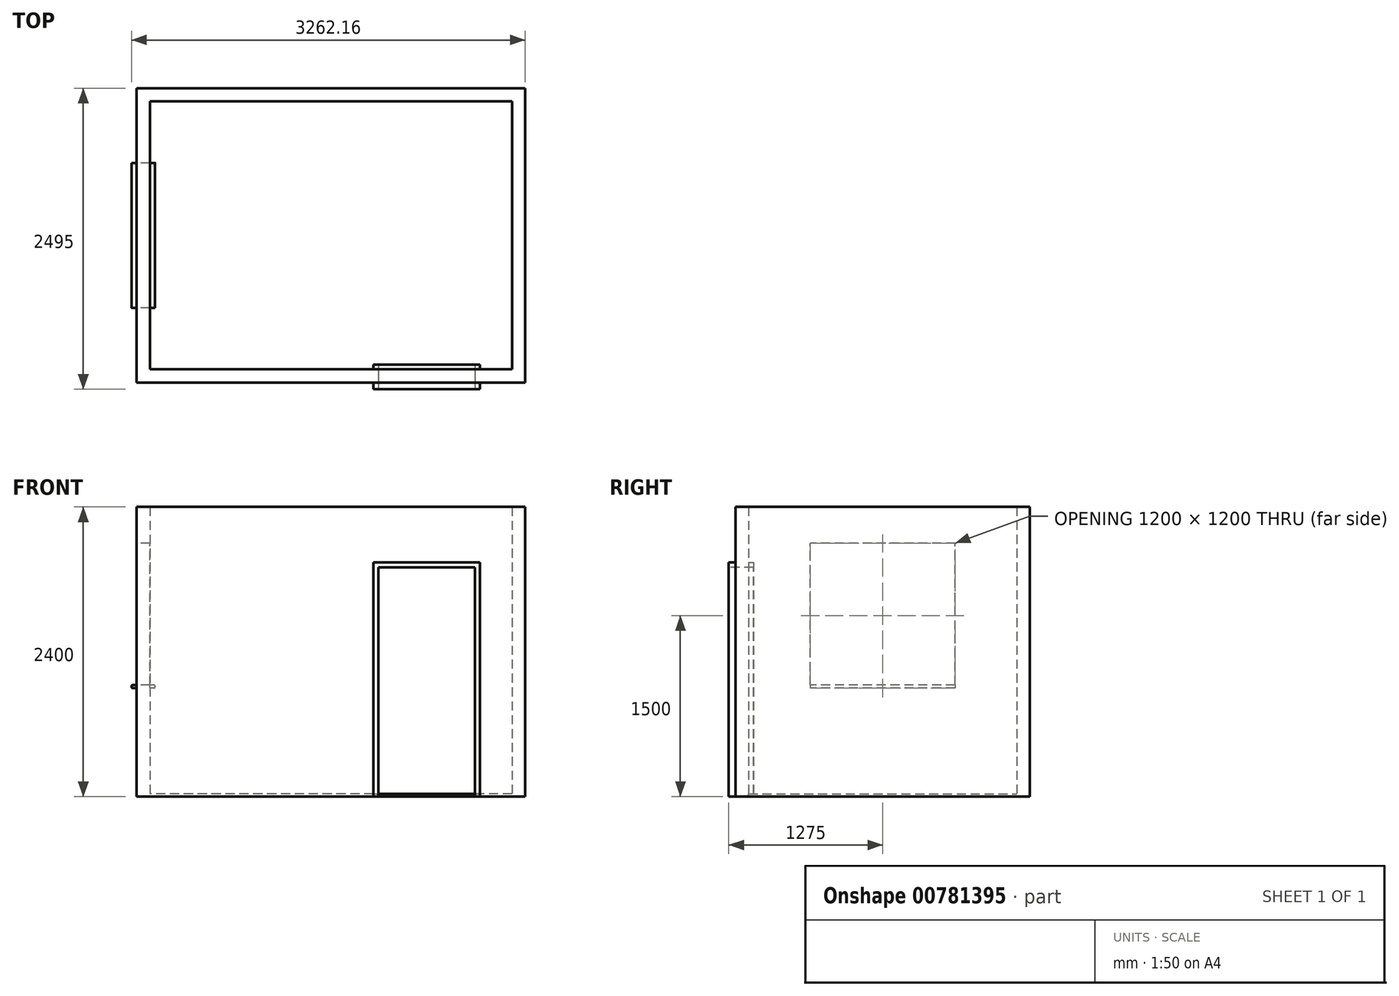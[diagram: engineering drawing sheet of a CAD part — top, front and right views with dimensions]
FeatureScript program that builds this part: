
annotation { "Feature Type Name" : "Feature", "Feature Type Description" : "" }
export const myFeature = defineFeature(function(context is Context, id is Id, definition is map)
    precondition{}
    {
        {
            var Q0;
            Q0=qCreatedBy(makeId("Top.planeOp"),FACE);
            var sketch = newSketch(context, id + "F0", { "sketchPlane" : qUnion([Q0])});
            skLineSegment(sketch, "E0.bottom", {"start": v(-1500, 1110) * mm, "end": v(1500, 1110) * mm});
            skLineSegment(sketch, "E0.top", {"start": v(-1500, -1110) * mm, "end": v(1500, -1110) * mm});
            skLineSegment(sketch, "E0.left", {"start": v(-1500, 1110) * mm, "end": v(-1500, -1110) * mm});
            skLineSegment(sketch, "E0.right", {"start": v(1500, 1110) * mm, "end": v(1500, -1110) * mm});
            skPoint(sketch, "E0.middle", {"position": v(0, 0) * mm});
            skLineSegment(sketch, "E1.0", {"start": v(1610, 1220) * mm, "end": v(1610, -1220) * mm});
            skLineSegment(sketch, "E1.1", {"start": v(-1610, 1220) * mm, "end": v(1610, 1220) * mm});
            skLineSegment(sketch, "E1.2", {"start": v(-1610, 1220) * mm, "end": v(-1610, -1220) * mm});
            skLineSegment(sketch, "E1.3", {"start": v(-1610, -1220) * mm, "end": v(1610, -1220) * mm});
            skSolve(sketch);
        }
        {
            var Q0;
            Q0 = qSketchRegion(id + "F0", true);
            var Q1;
            Q1=makeQuery(id+"F0.imprint","IMPRINT",FACE,{"disambiguationData":[TD([[makeQuery(id+"F0.imprint","IMPRINT",EDGE,{"derivedFrom":sQuery(id+"F0.wireOp",EDGE,"E0.bottom")}),-1.0]])]});
            extrude(context, id + "F1", {"entities" : qUnion([Q0, Q1]), "depth" : 25 * mm, "offsetDistance" : 25 * mm});
        }
        {
            var Q0;
            Q0 = qSketchRegion(id + "F0", true);
            extrude(context, id + "F2", {"entities" : qUnion([Q0]), "operationType" : NewBodyOperationType.ADD, "depth" : 2400 * mm, "offsetDistance" : 25 * mm});
        }
        {
            var Q0;
            {var subQ0=sQuery(id+"F0.wireOp",EDGE,"E1.3");Q0=makeQuery(id+"F2.boolean.opBoolean","MERGE",FACE,{"derivedFrom":[makeQuery(id+"F1.opExtrude","SWEPT_FACE",FACE,{"disambiguationData":[OSD([subQ0])]}),makeQuery(id+"F2.opExtrude","SWEPT_FACE",FACE,{"disambiguationData":[OSD([subQ0])]})]});}
            var sketch = newSketch(context, id + "F3", { "sketchPlane" : qUnion([Q0])});
            skLineSegment(sketch, "E2.bottom", {"start": v(1193, 0) * mm, "end": v(393, 0) * mm});
            skLineSegment(sketch, "E2.top", {"start": v(1193, 1900) * mm, "end": v(393, 1900) * mm});
            skLineSegment(sketch, "E2.left", {"start": v(1193, 0) * mm, "end": v(1193, 1900) * mm});
            skLineSegment(sketch, "E2.right", {"start": v(393, 0) * mm, "end": v(393, 1900) * mm});
            skLineSegment(sketch, "E3.bottom", {"start": v(353, 1940) * mm, "end": v(1233, 1940) * mm});
            skLineSegment(sketch, "E3.top", {"start": v(353, 0) * mm, "end": v(393, 0) * mm});
            skLineSegment(sketch, "E3.left", {"start": v(353, 1940) * mm, "end": v(353, 0) * mm});
            skLineSegment(sketch, "E3.right", {"start": v(1233, 1940) * mm, "end": v(1233, 0) * mm});
            skLineSegment(sketch, "E4.trimOffspring", {"start": v(1193, 0) * mm, "end": v(1233, 0) * mm});
            skSolve(sketch);
        }
        {
            var Q0;
            Q0=makeQuery(id+"F3.imprint","IMPRINT",FACE,{"disambiguationData":[TD([[makeQuery(id+"F3.imprint","IMPRINT",EDGE,{"derivedFrom":sQuery(id+"F3.wireOp",EDGE,"E2.bottom")}),1.0]])]});
            extrude(context, id + "F4", {"entities" : qUnion([Q0]), "operationType" : NewBodyOperationType.REMOVE, "oppositeDirection" : true, "depth" : 110 * mm, "offsetDistance" : 25 * mm});
        }
        {
            var Q0;
            Q0=makeQuery(id+"F3.imprint","IMPRINT",FACE,{"disambiguationData":[TD([[makeQuery(id+"F3.imprint","IMPRINT",EDGE,{"derivedFrom":sQuery(id+"F3.wireOp",EDGE,"E2.top")}),-1.0]])]});
            extrude(context, id + "F5", {"entities" : qUnion([Q0]), "operationType" : NewBodyOperationType.ADD, "depth" : 55 * mm, "offsetDistance" : 25 * mm, "hasSecondDirection" : true, "secondDirectionOppositeDirection" : true, "secondDirectionDepth" : 150 * mm});
        }
        {
            var Q0;
            {var subQ0=sQuery(id+"F0.wireOp",EDGE,"E1.2");Q0=makeQuery(id+"F2.boolean.opBoolean","MERGE",FACE,{"derivedFrom":[makeQuery(id+"F1.opExtrude","SWEPT_FACE",FACE,{"disambiguationData":[OSD([subQ0])]}),makeQuery(id+"F2.opExtrude","SWEPT_FACE",FACE,{"disambiguationData":[OSD([subQ0])]})]});}
            var sketch = newSketch(context, id + "F6", { "sketchPlane" : qUnion([Q0])});
            skLineSegment(sketch, "E5", {"start": v(0, 2400) * mm, "end": v(0, 0) * mm, "construction": true});
            skLineSegment(sketch, "E6", {"start": v(-1220, 1200) * mm, "end": v(1220, 1200) * mm, "construction": true});
            skLineSegment(sketch, "E7.bottom", {"start": v(-600, 2100) * mm, "end": v(600, 2100) * mm});
            skLineSegment(sketch, "E7.top", {"start": v(-600, 900) * mm, "end": v(600, 900) * mm});
            skLineSegment(sketch, "E7.left", {"start": v(-600, 2100) * mm, "end": v(-600, 900) * mm});
            skLineSegment(sketch, "E7.right", {"start": v(600, 2100) * mm, "end": v(600, 900) * mm});
            skPoint(sketch, "E7.middle", {"position": v(0, 1500) * mm});
            skSolve(sketch);
        }
        {
            var Q0;
            Q0=makeQuery(id+"F6.imprint","IMPRINT",FACE,{"disambiguationData":[TD([[makeQuery(id+"F6.imprint","IMPRINT",EDGE,{"derivedFrom":sQuery(id+"F6.wireOp",EDGE,"E7.bottom")}),-1.0]])]});
            extrude(context, id + "F7", {"entities" : qUnion([Q0]), "operationType" : NewBodyOperationType.REMOVE, "oppositeDirection" : true, "depth" : 2505 * mm, "offsetDistance" : 25 * mm});
        }
        {
            var Q0;
            Q0=makeQuery(id+"F7.boolean.opBoolean","COPY",FACE,{"derivedFrom":makeQuery(id+"F7.opExtrude","SWEPT_FACE",FACE,{"disambiguationData":[OSD([sQuery(id+"F6.wireOp",EDGE,"E7.top")])]})});
            var sketch = newSketch(context, id + "F8", { "sketchPlane" : qUnion([Q0])});
            skLineSegment(sketch, "E8", {"start": v(-1500, 0) * mm, "end": v(-1610, 0) * mm, "construction": true});
            skLineSegment(sketch, "E9.bottom", {"start": v(-1457.84, 600) * mm, "end": v(-1652.16, 600) * mm});
            skLineSegment(sketch, "E9.top", {"start": v(-1457.84, -600) * mm, "end": v(-1652.16, -600) * mm});
            skLineSegment(sketch, "E9.left", {"start": v(-1457.84, 600) * mm, "end": v(-1457.84, -600) * mm});
            skLineSegment(sketch, "E9.right", {"start": v(-1652.16, 600) * mm, "end": v(-1652.16, -600) * mm});
            skPoint(sketch, "E9.middle", {"position": v(-1555, 0) * mm});
            skSolve(sketch);
        }
        {
            var Q0;
            Q0 = qSketchRegion(id + "F8", true);
            extrude(context, id + "F9", {"entities" : qUnion([Q0]), "operationType" : NewBodyOperationType.ADD, "depth" : 25 * mm, "offsetDistance" : 25 * mm});
        }
        {
            var Q0;
            Q0=makeQuery(id+"F9.opExtrude","CAP_EDGE",EDGE,{"disambiguationData":[OSD([sQuery(id+"F8.wireOp",EDGE,"E9.left")])],"isStart":false});
            var Q1;
            Q1=makeQuery(id+"F9.opExtrude","CAP_EDGE",EDGE,{"disambiguationData":[OSD([sQuery(id+"F8.wireOp",EDGE,"E9.left")])],"isStart":true});
            var Q2;
            Q2=makeQuery(id+"F9.opExtrude","CAP_EDGE",EDGE,{"disambiguationData":[OSD([sQuery(id+"F8.wireOp",EDGE,"E9.right")])],"isStart":false});
            var Q3;
            Q3=makeQuery(id+"F9.opExtrude","CAP_EDGE",EDGE,{"disambiguationData":[OSD([sQuery(id+"F8.wireOp",EDGE,"E9.right")])],"isStart":true});
            fillet(context, id + "F10", {"entities" : qUnion([Q0, Q1, Q2, Q3]), "radius" : 10 * mm, "tangentPropagation" : true, "allowEdgeOverflow" : false});
        }
    });
